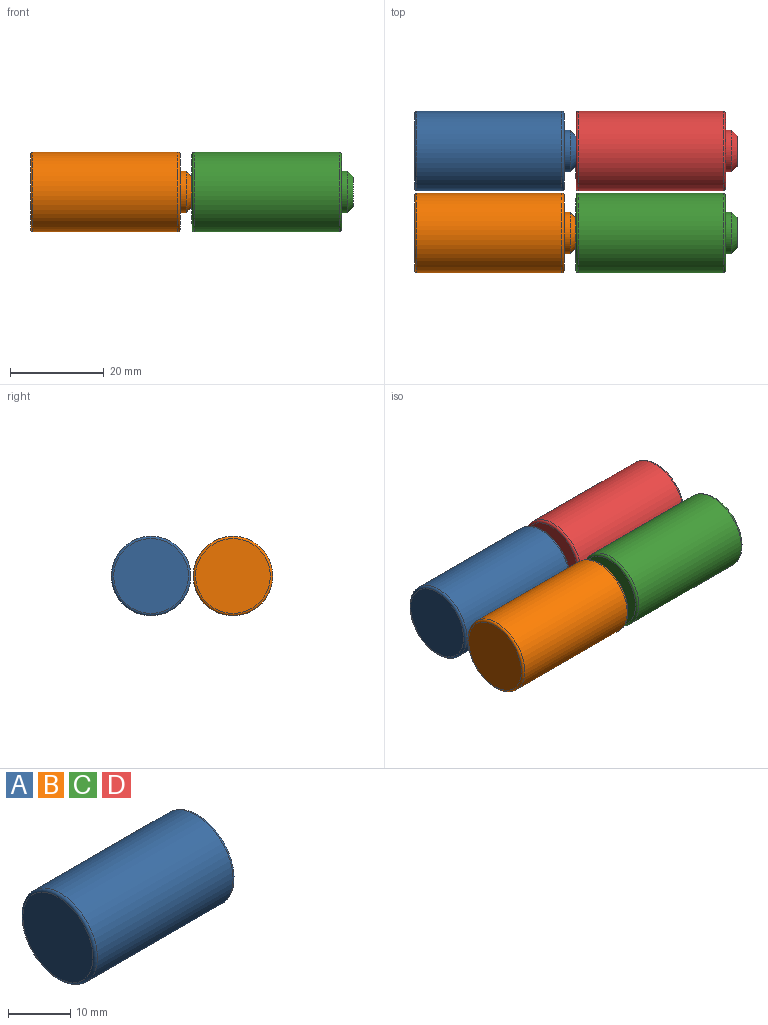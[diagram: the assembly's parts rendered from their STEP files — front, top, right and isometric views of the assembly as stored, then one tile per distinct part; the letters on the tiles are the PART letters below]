
ASSEMBLY  parts=4 mates=6
PART A: 8 faces, bbox 34.5x18.4x18.4 mm
  f0: cylinder r=8.5mm len=30.94mm, axis (-1,0,0), area 1652.6mm2, adj f6,f7
  f1: plane 15.98x15.98mm, normal (-1,0,0), area 200.7mm2, adj f7
  f2: plane 15.98x15.98mm, normal (1,0,0), area 137.8mm2, adj f3,f6
  f3: cylinder r=4.47mm len=8.95mm, axis (1,0,0), area 35.7mm2, adj f2,f5
  f4: plane 6.41x6.41mm, normal (1,0,0), area 32.2mm2, adj f5
  f5: cone r=3.2mm half-angle=45deg, axis (-1,0,0), area 43.3mm2, adj f3,f4
  f6: torus R=7.99mm, axis (1,0,0), area 41.7mm2, adj f0,f2
  f7: torus R=7.99mm, axis (1,0,0), area 41.7mm2, adj f0,f1
PART B: same geometry as A
PART C: same geometry as A
PART D: same geometry as A
PLACE A rot(axis=(-0.98,-0.17,-0.13),0deg) t=(-21.22,29.74,4.98)mm
PLACE B t=(-21.22,12.24,4.98)mm
PLACE C t=(13.28,12.24,4.98)mm
PLACE D t=(13.28,29.74,4.98)mm
MATE planar D.f0 <-> A.f0  axis (-1,0,0) through (13.28,11.93,-18.61)mm
MATE cylindrical B.f0 <-> C.f0  axis (-1,0,0) through (-5.24,-5.57,-18.61)mm
MATE fastened D.f0 <-> C.f4  axis (1,0,0) through (47.78,11.93,-18.61)mm
MATE cylindrical A.f0 <-> D.f0  axis (-1,0,0) through (-5.24,11.93,-18.61)mm
MATE planar C.f0 <-> D.f0  axis (1,0,0) through (45.24,-5.57,-18.61)mm
MATE planar B.f0 <-> C.f0  axis (1,0,0) through (13.28,-5.57,-18.61)mm
